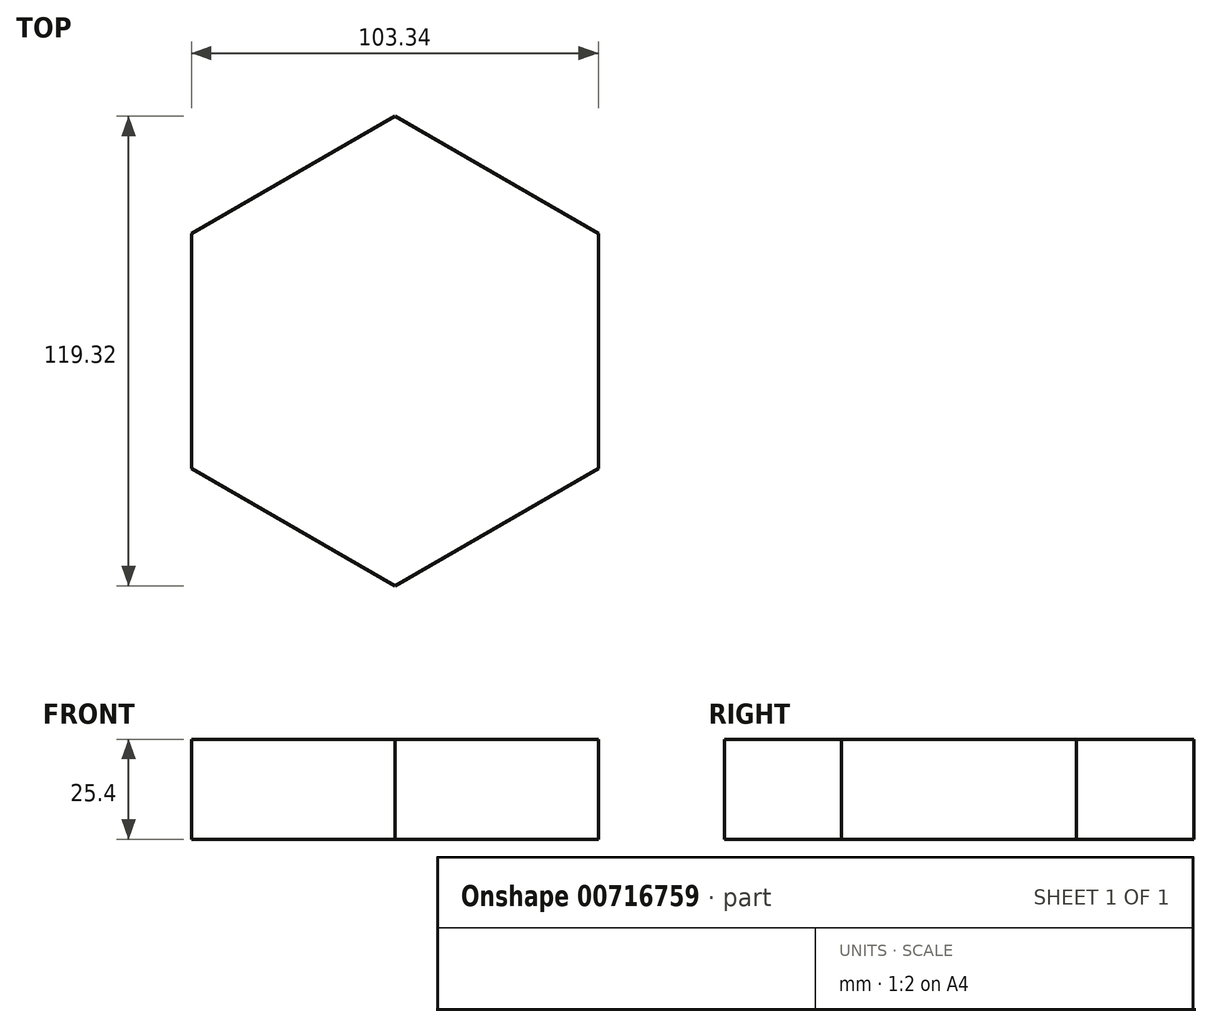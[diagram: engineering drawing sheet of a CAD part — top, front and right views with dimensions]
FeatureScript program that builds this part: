
annotation { "Feature Type Name" : "Feature", "Feature Type Description" : "" }
export const myFeature = defineFeature(function(context is Context, id is Id, definition is map)
    precondition{}
    {
        {
            var Q0;
            Q0=qCreatedBy(makeId("Top.planeOp"),FACE);
            var sketch = newSketch(context, id + "F0", { "sketchPlane" : qUnion([Q0])});
            skCircle(sketch, "E0.cCircle", {"center": v(0, 0) * mm, "radius": 51.67 * mm, "construction": true});
            skLineSegment(sketch, "E0.0", {"start": v(-51.67, -29.83) * mm, "end": v(-51.67, 29.83) * mm});
            skLineSegment(sketch, "E0.1", {"start": v(-51.67, 29.83) * mm, "end": v(0, 59.66) * mm});
            skLineSegment(sketch, "E0.2", {"start": v(0, 59.66) * mm, "end": v(51.67, 29.83) * mm});
            skLineSegment(sketch, "E0.3", {"start": v(51.67, 29.83) * mm, "end": v(51.67, -29.83) * mm});
            skLineSegment(sketch, "E0.4", {"start": v(51.67, -29.83) * mm, "end": v(0, -59.66) * mm});
            skLineSegment(sketch, "E0.5", {"start": v(0, -59.66) * mm, "end": v(-51.67, -29.83) * mm});
            skPoint(sketch, "E0.0.midPoint", {"position": v(-51.67, 0) * mm});
            skSolve(sketch);
        }
        {
            var Q0;
            Q0 = qSketchRegion(id + "F0", true);
            extrude(context, id + "F1", {"entities" : qUnion([Q0]), "depth" : 25.4 * mm, "offsetDistance" : 25.4 * mm});
        }
    });
